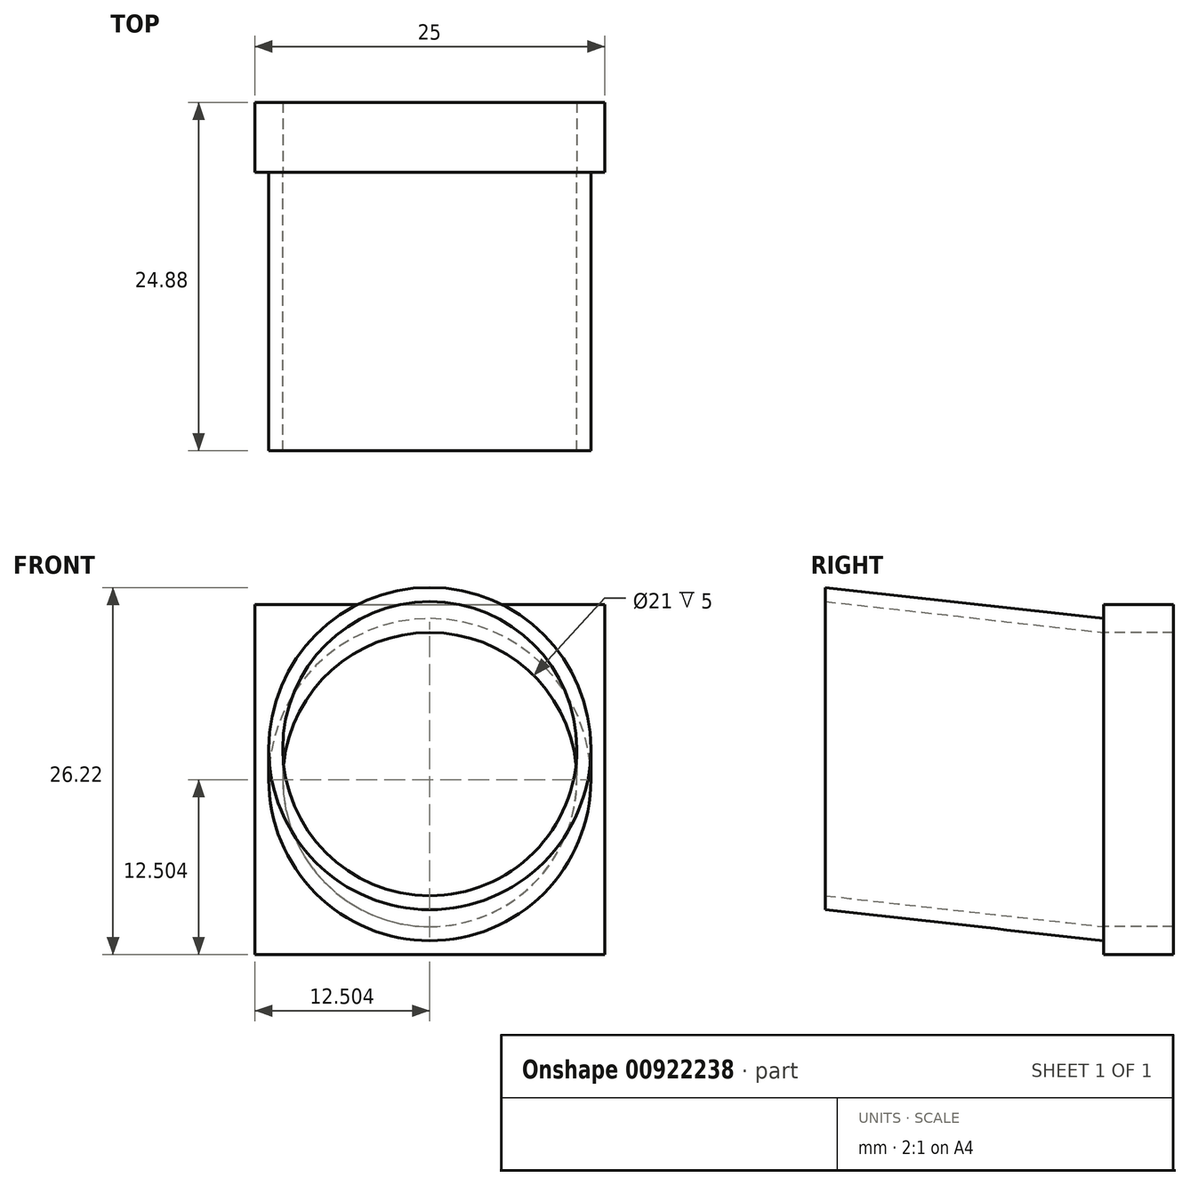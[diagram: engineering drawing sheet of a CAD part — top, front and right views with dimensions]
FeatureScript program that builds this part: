
annotation { "Feature Type Name" : "Feature", "Feature Type Description" : "" }
export const myFeature = defineFeature(function(context is Context, id is Id, definition is map)
    precondition{}
    {
        {
            var Q0;
            Q0=qCreatedBy(makeId("Front.planeOp"),FACE);
            var sketch = newSketch(context, id + "F0", { "sketchPlane" : qUnion([Q0])});
            skLineSegment(sketch, "E0.bottom", {"start": v(-19.76, 20.84) * mm, "end": v(5.24, 20.84) * mm});
            skLineSegment(sketch, "E0.top", {"start": v(-19.76, -4.16) * mm, "end": v(5.24, -4.16) * mm});
            skLineSegment(sketch, "E0.left", {"start": v(-19.76, 20.84) * mm, "end": v(-19.76, -4.16) * mm});
            skLineSegment(sketch, "E0.right", {"start": v(5.24, 20.84) * mm, "end": v(5.24, -4.16) * mm});
            skSolve(sketch);
        }
        {
            var Q0;
            Q0=makeQuery(id+"F0.imprint","IMPRINT",FACE,{"disambiguationData":[TD([[makeQuery(id+"F0.imprint","IMPRINT",EDGE,{"derivedFrom":sQuery(id+"F0.wireOp",EDGE,"E0.bottom")}),-1.0]])]});
            var sketch = newSketch(context, id + "F1", { "sketchPlane" : qUnion([Q0])});
            skCircle(sketch, "E1", {"center": v(-7.26, 8.34) * mm, "radius": 10.5 * mm});
            skCircle(sketch, "E2", {"center": v(-7.26, 8.34) * mm, "radius": 11.5 * mm});
            skSolve(sketch);
        }
        {
            var Q0;
            Q0=qCreatedBy(makeId("Right.planeOp"),FACE);
            var sketch = newSketch(context, id + "F2", { "sketchPlane" : qUnion([Q0])});
            skLineSegment(sketch, "E3", {"start": v(0, 8.34) * mm, "end": v(-19.88, 10.56) * mm});
            skSolve(sketch);
        }
        {
            var Q0;
            Q0=makeQuery(id+"F1.imprint","IMPRINT",FACE,{"disambiguationData":[TD([[makeQuery(id+"F1.imprint","IMPRINT",EDGE,{"derivedFrom":sQuery(id+"F1.wireOp",EDGE,"E1")}),-1.0]])]});
            var Q1;
            Q1 = qConstructionFilter(qBodyType(qCreatedBy(id + "F2" ,EDGE), BodyType.WIRE), ConstructionObject.NO);
            sweep(context, id + "F3", {"profiles" : qUnion([Q0]), "path" : qUnion([Q1])});
        }
        {
            var Q0;
            Q0=makeQuery(id+"F0.imprint","IMPRINT",FACE,{"disambiguationData":[TD([[makeQuery(id+"F0.imprint","IMPRINT",EDGE,{"derivedFrom":sQuery(id+"F0.wireOp",EDGE,"E0.bottom")}),-1.0]])]});
            extrude(context, id + "F4", {"entities" : qUnion([Q0]), "operationType" : NewBodyOperationType.ADD, "oppositeDirection" : true, "depth" : 5 * mm, "offsetDistance" : 25 * mm});
        }
        {
            var Q0;
            {var subQ0=sQuery(id+"F0.wireOp",EDGE,"E0.left");var subQ1=sQuery(id+"F0.wireOp",EDGE,"E0.top");var subQ2=sQuery(id+"F0.wireOp",EDGE,"E0.bottom");var subQ3=sQuery(id+"F0.wireOp",EDGE,"E0.right");Q0=makeQuery(id+"F4.boolean.opBoolean","SPLIT",FACE,{"disambiguationData":[TD([makeQuery(id+"F4.opExtrude","SWEPT_FACE",FACE,{"disambiguationData":[OSD([subQ2])]})])],"derivedFrom":makeQuery(id+"F4.opExtrude","CAP_FACE",FACE,{"disambiguationData":[OSD([subQ2,subQ1,subQ0,subQ3])],"isStart":true})});}
            var sketch = newSketch(context, id + "F5", { "sketchPlane" : qUnion([Q0])});
            skCircle(sketch, "E4", {"center": v(-7.26, 8.34) * mm, "radius": 10.5 * mm});
            skSolve(sketch);
        }
        {
            var Q0;
            Q0 = qSketchRegion(id + "F5", true);
            extrude(context, id + "F6", {"entities" : qUnion([Q0]), "operationType" : NewBodyOperationType.REMOVE, "endBound" : BoundingType.THROUGH_ALL, "oppositeDirection" : true, "depth" : 25 * mm, "offsetDistance" : 25 * mm});
        }
    });
